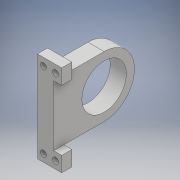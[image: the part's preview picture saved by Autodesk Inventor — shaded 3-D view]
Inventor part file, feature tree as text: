
AUTODESK INVENTOR PART (.ipt)
format: ipt  version: 2017 (Build 210142000, 142)  size: 171,008 bytes
history: native  units: mm
features: extrude x3, sketch x3
ambient origin geometry x8: Origin, YZ Plane, XZ Plane, XY Plane, X Axis, Y Axis, Z Axis, Center Point
bodies: Solid1 (feature_tree)
feature tree (6):
  extrude  "Extrusion1"  Depth=27.5mm
  extrude  "Extrusion2"  TaperAngle=180.0deg  [1 undecoded]
  extrude  "Extrusion3"  Depth=5.0mm
  sketch  "Sketch1"  dims[d0=22.0mm d1=27.5mm]
  sketch  "Sketch3"  dims[d2=25.0mm d3=180.0deg]
  sketch  "Sketch4"  dims[d4=20.0mm d7=5.0mm d8=5.0mm d9=5.0mm d10=5.0mm d11=30.0mm d12=8.0mm d13=0.0mm d14=5.0mm d15=7.5mm d16=5.0mm d17=7.5mm d22=4.0mm d23=0.0mm d24=3.0mm d25=3.0mm d26=0.0mm d27=3.0mm d28=3.0mm d29=5.0mm d30=0.0mm]
note: 1 required parameter value undecoded (feature->parameter linkage not recoverable at this tier; creation-order binding heuristic only, values carry confidence <= 0.55)
